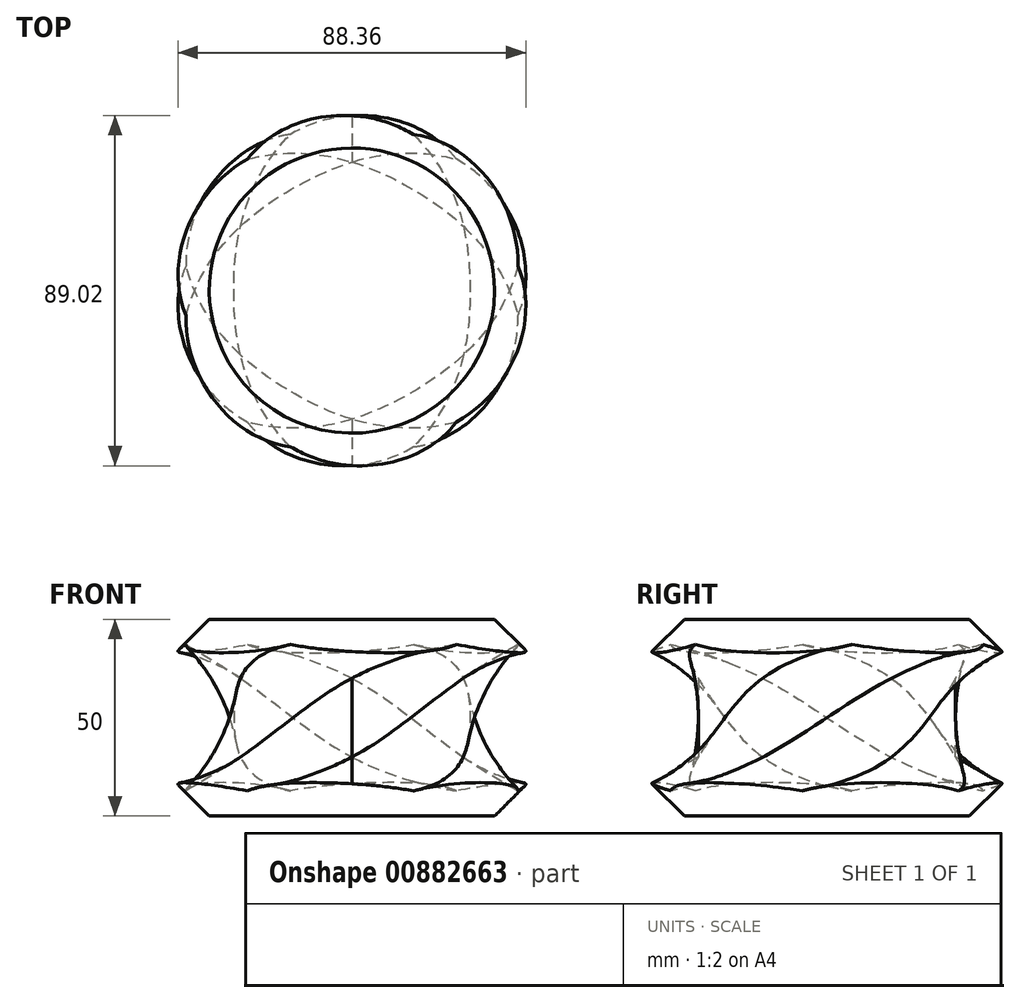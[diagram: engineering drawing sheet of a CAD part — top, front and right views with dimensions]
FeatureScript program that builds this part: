
annotation { "Feature Type Name" : "Feature", "Feature Type Description" : "" }
export const myFeature = defineFeature(function(context is Context, id is Id, definition is map)
    precondition{}
    {
        {
            var Q0;
            Q0=qCreatedBy(makeId("Front.planeOp"),FACE);
            var sketch = newSketch(context, id + "F0", { "sketchPlane" : qUnion([Q0])});
            skCircle(sketch, "E0.cCircle", {"center": v(-50, 0) * mm, "radius": 17.32 * mm, "construction": true});
            skLineSegment(sketch, "E0.0", {"start": v(-60, 17.32) * mm, "end": v(-40, 17.32) * mm});
            skLineSegment(sketch, "E0.1", {"start": v(-40, 17.32) * mm, "end": v(-30, 0) * mm});
            skLineSegment(sketch, "E0.2", {"start": v(-30, 0) * mm, "end": v(-40, -17.32) * mm});
            skLineSegment(sketch, "E0.3", {"start": v(-40, -17.32) * mm, "end": v(-60, -17.32) * mm});
            skLineSegment(sketch, "E0.4", {"start": v(-60, -17.32) * mm, "end": v(-70, 0) * mm});
            skLineSegment(sketch, "E0.5", {"start": v(-70, 0) * mm, "end": v(-60, 17.32) * mm});
            skPoint(sketch, "E0.0.midPoint", {"position": v(-50, 17.32) * mm});
            skLineSegment(sketch, "E1", {"start": v(0, 0) * mm, "end": v(-30.77, 0) * mm, "construction": true});
            skLineSegment(sketch, "E2", {"start": v(0, 0) * mm, "end": v(0, 28.34) * mm, "construction": true});
            skCircle(sketch, "E3.cCircle", {"center": v(50, 0) * mm, "radius": 17.32 * mm, "construction": true});
            skLineSegment(sketch, "E3.0", {"start": v(60, -17.32) * mm, "end": v(40, -17.32) * mm});
            skLineSegment(sketch, "E3.1", {"start": v(40, -17.32) * mm, "end": v(30, 0) * mm});
            skLineSegment(sketch, "E3.2", {"start": v(30, 0) * mm, "end": v(40, 17.32) * mm});
            skLineSegment(sketch, "E3.3", {"start": v(40, 17.32) * mm, "end": v(60, 17.32) * mm});
            skLineSegment(sketch, "E3.4", {"start": v(60, 17.32) * mm, "end": v(70, 0) * mm});
            skLineSegment(sketch, "E3.5", {"start": v(70, 0) * mm, "end": v(60, -17.32) * mm});
            skPoint(sketch, "E3.0.midPoint", {"position": v(50, -17.32) * mm});
            skSolve(sketch);
        }
        {
            var Q0;
            Q0=sQuery(id+"F0.wireOp",EDGE,"E2");
            var Q1;
            Q1=sQuery(id+"F0.wireOp",EDGE,"E1");
            cPlane(context, id + "F1", {"entities" : qUnion([Q0, Q1]), "cplaneType" : CPlaneType.LINE_ANGLE, "offset" : 150 * mm, "angle" : 150 * degree, "width" : 150 * mm, "height" : 150 * mm});
        }
        {
            var Q0;
            Q0=sQuery(id+"F0.wireOp",EDGE,"E2");
            var Q1;
            Q1=sQuery(id+"F0.wireOp",EDGE,"E1");
            cPlane(context, id + "F2", {"entities" : qUnion([Q0, Q1]), "cplaneType" : CPlaneType.LINE_ANGLE, "offset" : 150 * mm, "angle" : 120 * degree, "width" : 150 * mm, "height" : 150 * mm});
        }
        {
            var Q0;
            Q0=sQuery(id+"F0.wireOp",EDGE,"E2");
            var Q1;
            Q1=sQuery(id+"F0.wireOp",EDGE,"E1");
            cPlane(context, id + "F3", {"entities" : qUnion([Q0, Q1]), "cplaneType" : CPlaneType.LINE_ANGLE, "offset" : 150 * mm, "angle" : 60 * degree, "width" : 150 * mm, "height" : 150 * mm});
        }
        {
            var Q0;
            Q0=sQuery(id+"F0.wireOp",EDGE,"E2");
            var Q1;
            Q1=sQuery(id+"F0.wireOp",EDGE,"E1");
            cPlane(context, id + "F4", {"entities" : qUnion([Q0, Q1]), "cplaneType" : CPlaneType.LINE_ANGLE, "offset" : 150 * mm, "angle" : 30 * degree, "width" : 150 * mm, "height" : 150 * mm});
        }
        {
            var Q0;
            Q0=qCreatedBy(id+"F1.planeOp",FACE);
            var sketch = newSketch(context, id + "F5", { "sketchPlane" : qUnion([Q0])});
            skCircle(sketch, "E4.cCircle", {"center": v(50, 0) * mm, "radius": 17.32 * mm, "construction": true});
            skLineSegment(sketch, "E4.0", {"start": v(32.68, 10) * mm, "end": v(50, 20) * mm});
            skLineSegment(sketch, "E4.1", {"start": v(50, 20) * mm, "end": v(67.32, 10) * mm});
            skLineSegment(sketch, "E4.2", {"start": v(67.32, 10) * mm, "end": v(67.32, -10) * mm});
            skLineSegment(sketch, "E4.3", {"start": v(67.32, -10) * mm, "end": v(50, -20) * mm});
            skLineSegment(sketch, "E4.4", {"start": v(50, -20) * mm, "end": v(32.68, -10) * mm});
            skLineSegment(sketch, "E4.5", {"start": v(32.68, -10) * mm, "end": v(32.68, 10) * mm});
            skPoint(sketch, "E4.0.midPoint", {"position": v(41.34, 15) * mm});
            skLineSegment(sketch, "E5.MirrorCS", {"start": v(-32.68, 10) * mm, "end": v(-50, 20) * mm});
            skPoint(sketch, "E6.MirrorP", {"position": v(-41.34, 15) * mm});
            skLineSegment(sketch, "E7.MirrorCS", {"start": v(-32.68, -10) * mm, "end": v(-32.68, 10) * mm});
            skLineSegment(sketch, "E8.MirrorCS", {"start": v(-50, -20) * mm, "end": v(-32.68, -10) * mm});
            skLineSegment(sketch, "E9.MirrorCS", {"start": v(-67.32, -10) * mm, "end": v(-50, -20) * mm});
            skLineSegment(sketch, "E10.MirrorCS", {"start": v(-67.32, 10) * mm, "end": v(-67.32, -10) * mm});
            skLineSegment(sketch, "E11.MirrorCS", {"start": v(-50, 20) * mm, "end": v(-67.32, 10) * mm});
            skCircle(sketch, "E12.MirrorC", {"center": v(-50, 0) * mm, "radius": 17.32 * mm, "construction": true});
            skSolve(sketch);
        }
        {
            var Q0;
            Q0=qCreatedBy(id+"F2.planeOp",FACE);
            var sketch = newSketch(context, id + "F6", { "sketchPlane" : qUnion([Q0])});
            skCircle(sketch, "E13.cCircle", {"center": v(50, 0) * mm, "radius": 17.32 * mm, "construction": true});
            skLineSegment(sketch, "E13.0", {"start": v(30, 0) * mm, "end": v(40, 17.32) * mm});
            skLineSegment(sketch, "E13.1", {"start": v(40, 17.32) * mm, "end": v(60, 17.32) * mm});
            skLineSegment(sketch, "E13.2", {"start": v(60, 17.32) * mm, "end": v(70, 0) * mm});
            skLineSegment(sketch, "E13.3", {"start": v(70, 0) * mm, "end": v(60, -17.32) * mm});
            skLineSegment(sketch, "E13.4", {"start": v(60, -17.32) * mm, "end": v(40, -17.32) * mm});
            skLineSegment(sketch, "E13.5", {"start": v(40, -17.32) * mm, "end": v(30, 0) * mm});
            skPoint(sketch, "E13.0.midPoint", {"position": v(35, 8.66) * mm});
            skLineSegment(sketch, "E14.MirrorCS", {"start": v(-40, 17.32) * mm, "end": v(-60, 17.32) * mm});
            skLineSegment(sketch, "E15.MirrorCS", {"start": v(-30, 0) * mm, "end": v(-40, 17.32) * mm});
            skLineSegment(sketch, "E16.MirrorCS", {"start": v(-40, -17.32) * mm, "end": v(-30, 0) * mm});
            skLineSegment(sketch, "E17.MirrorCS", {"start": v(-60, -17.32) * mm, "end": v(-40, -17.32) * mm});
            skLineSegment(sketch, "E18.MirrorCS", {"start": v(-70, 0) * mm, "end": v(-60, -17.32) * mm});
            skLineSegment(sketch, "E19.MirrorCS", {"start": v(-60, 17.32) * mm, "end": v(-70, 0) * mm});
            skCircle(sketch, "E20.MirrorC", {"center": v(-50, 0) * mm, "radius": 17.32 * mm, "construction": true});
            skPoint(sketch, "E21.MirrorP", {"position": v(-35, 8.66) * mm});
            skSolve(sketch);
        }
        {
            var Q0;
            Q0=qCreatedBy(makeId("Right.planeOp"),FACE);
            var sketch = newSketch(context, id + "F7", { "sketchPlane" : qUnion([Q0])});
            skCircle(sketch, "E22.cCircle", {"center": v(50, 0) * mm, "radius": 17.32 * mm, "construction": true});
            skLineSegment(sketch, "E22.0", {"start": v(32.68, -10) * mm, "end": v(32.68, 10) * mm});
            skLineSegment(sketch, "E22.1", {"start": v(32.68, 10) * mm, "end": v(50, 20) * mm});
            skLineSegment(sketch, "E22.2", {"start": v(50, 20) * mm, "end": v(67.32, 10) * mm});
            skLineSegment(sketch, "E22.3", {"start": v(67.32, 10) * mm, "end": v(67.32, -10) * mm});
            skLineSegment(sketch, "E22.4", {"start": v(67.32, -10) * mm, "end": v(50, -20) * mm});
            skLineSegment(sketch, "E22.5", {"start": v(50, -20) * mm, "end": v(32.68, -10) * mm});
            skPoint(sketch, "E22.0.midPoint", {"position": v(32.68, 0) * mm});
            skLineSegment(sketch, "E23", {"start": v(0, 0) * mm, "end": v(18.07, 0) * mm, "construction": true});
            skLineSegment(sketch, "E24.MirrorCS", {"start": v(-50, 20) * mm, "end": v(-67.32, 10) * mm});
            skLineSegment(sketch, "E25.MirrorCS", {"start": v(-67.32, 10) * mm, "end": v(-67.32, -10) * mm});
            skLineSegment(sketch, "E26.MirrorCS", {"start": v(-67.32, -10) * mm, "end": v(-50, -20) * mm});
            skLineSegment(sketch, "E27.MirrorCS", {"start": v(-50, -20) * mm, "end": v(-32.68, -10) * mm});
            skPoint(sketch, "E28.MirrorP", {"position": v(-32.68, 0) * mm});
            skCircle(sketch, "E29.MirrorC", {"center": v(-50, 0) * mm, "radius": 17.32 * mm, "construction": true});
            skLineSegment(sketch, "E30.MirrorCS", {"start": v(-32.68, -10) * mm, "end": v(-32.68, 10) * mm});
            skLineSegment(sketch, "E31.MirrorCS", {"start": v(-32.68, 10) * mm, "end": v(-50, 20) * mm});
            skSolve(sketch);
        }
        {
            var Q0;
            Q0=qCreatedBy(id+"F3.planeOp",FACE);
            var sketch = newSketch(context, id + "F8", { "sketchPlane" : qUnion([Q0])});
            skCircle(sketch, "E32.cCircle", {"center": v(50, 0) * mm, "radius": 17.32 * mm, "construction": true});
            skLineSegment(sketch, "E32.0", {"start": v(40, -17.32) * mm, "end": v(30, 0) * mm});
            skLineSegment(sketch, "E32.1", {"start": v(30, 0) * mm, "end": v(40, 17.32) * mm});
            skLineSegment(sketch, "E32.2", {"start": v(40, 17.32) * mm, "end": v(60, 17.32) * mm});
            skLineSegment(sketch, "E32.3", {"start": v(60, 17.32) * mm, "end": v(70, 0) * mm});
            skLineSegment(sketch, "E32.4", {"start": v(70, 0) * mm, "end": v(60, -17.32) * mm});
            skLineSegment(sketch, "E32.5", {"start": v(60, -17.32) * mm, "end": v(40, -17.32) * mm});
            skPoint(sketch, "E32.0.midPoint", {"position": v(35, -8.66) * mm});
            skLineSegment(sketch, "E33.MirrorCS", {"start": v(-40, -17.32) * mm, "end": v(-30, 0) * mm});
            skCircle(sketch, "E34.MirrorC", {"center": v(-50, 0) * mm, "radius": 17.32 * mm, "construction": true});
            skPoint(sketch, "E35.MirrorP", {"position": v(-35, -8.66) * mm});
            skLineSegment(sketch, "E36.MirrorCS", {"start": v(-60, -17.32) * mm, "end": v(-40, -17.32) * mm});
            skLineSegment(sketch, "E37.MirrorCS", {"start": v(-70, 0) * mm, "end": v(-60, -17.32) * mm});
            skLineSegment(sketch, "E38.MirrorCS", {"start": v(-60, 17.32) * mm, "end": v(-70, 0) * mm});
            skLineSegment(sketch, "E39.MirrorCS", {"start": v(-40, 17.32) * mm, "end": v(-60, 17.32) * mm});
            skLineSegment(sketch, "E40.MirrorCS", {"start": v(-30, 0) * mm, "end": v(-40, 17.32) * mm});
            skSolve(sketch);
        }
        {
            var Q0;
            Q0=qCreatedBy(id+"F4.planeOp",FACE);
            var sketch = newSketch(context, id + "F9", { "sketchPlane" : qUnion([Q0])});
            skCircle(sketch, "E41.cCircle", {"center": v(50, 0) * mm, "radius": 17.32 * mm, "construction": true});
            skLineSegment(sketch, "E41.0", {"start": v(50, -20) * mm, "end": v(32.68, -10) * mm});
            skLineSegment(sketch, "E41.1", {"start": v(32.68, -10) * mm, "end": v(32.68, 10) * mm});
            skLineSegment(sketch, "E41.2", {"start": v(32.68, 10) * mm, "end": v(50, 20) * mm});
            skLineSegment(sketch, "E41.3", {"start": v(50, 20) * mm, "end": v(67.32, 10) * mm});
            skLineSegment(sketch, "E41.4", {"start": v(67.32, 10) * mm, "end": v(67.32, -10) * mm});
            skLineSegment(sketch, "E41.5", {"start": v(67.32, -10) * mm, "end": v(50, -20) * mm});
            skPoint(sketch, "E41.0.midPoint", {"position": v(41.34, -15) * mm});
            skLineSegment(sketch, "E42.MirrorCS", {"start": v(-67.32, -10) * mm, "end": v(-50, -20) * mm});
            skLineSegment(sketch, "E43.MirrorCS", {"start": v(-50, 20) * mm, "end": v(-67.32, 10) * mm});
            skLineSegment(sketch, "E44.MirrorCS", {"start": v(-50, -20) * mm, "end": v(-32.68, -10) * mm});
            skLineSegment(sketch, "E45.MirrorCS", {"start": v(-67.32, 10) * mm, "end": v(-67.32, -10) * mm});
            skLineSegment(sketch, "E46.MirrorCS", {"start": v(-32.68, 10) * mm, "end": v(-50, 20) * mm});
            skLineSegment(sketch, "E47.MirrorCS", {"start": v(-32.68, -10) * mm, "end": v(-32.68, 10) * mm});
            skCircle(sketch, "E48.MirrorC", {"center": v(-50, 0) * mm, "radius": 17.32 * mm, "construction": true});
            skPoint(sketch, "E49.MirrorP", {"position": v(-41.34, -15) * mm});
            skSolve(sketch);
        }
        {
            var Q0;
            Q0=makeQuery(id+"F0.imprint","IMPRINT",FACE,{"disambiguationData":[TD([[makeQuery(id+"F0.imprint","IMPRINT",EDGE,{"derivedFrom":sQuery(id+"F0.wireOp",EDGE,"E0.0")}),-1.0]])]});
            var Q1;
            Q1=makeQuery(id+"F5.imprint","IMPRINT",FACE,{"disambiguationData":[TD([[makeQuery(id+"F5.imprint","IMPRINT",EDGE,{"derivedFrom":sQuery(id+"F5.wireOp",EDGE,"E4.0")}),-1.0]])]});
            var Q2;
            Q2=makeQuery(id+"F6.imprint","IMPRINT",FACE,{"disambiguationData":[TD([[makeQuery(id+"F6.imprint","IMPRINT",EDGE,{"derivedFrom":sQuery(id+"F6.wireOp",EDGE,"E13.0")}),-1.0]])]});
            var Q3;
            Q3=makeQuery(id+"F7.imprint","IMPRINT",FACE,{"disambiguationData":[TD([[makeQuery(id+"F7.imprint","IMPRINT",EDGE,{"derivedFrom":sQuery(id+"F7.wireOp",EDGE,"E22.0")}),-1.0]])]});
            var Q4;
            Q4=makeQuery(id+"F8.imprint","IMPRINT",FACE,{"disambiguationData":[TD([[makeQuery(id+"F8.imprint","IMPRINT",EDGE,{"derivedFrom":sQuery(id+"F8.wireOp",EDGE,"E32.0")}),-1.0]])]});
            var Q5;
            Q5=makeQuery(id+"F9.imprint","IMPRINT",FACE,{"disambiguationData":[TD([[makeQuery(id+"F9.imprint","IMPRINT",EDGE,{"derivedFrom":sQuery(id+"F9.wireOp",EDGE,"E41.0")}),-1.0]])]});
            var Q6;
            Q6=makeQuery(id+"F0.imprint","IMPRINT",FACE,{"disambiguationData":[TD([[makeQuery(id+"F0.imprint","IMPRINT",EDGE,{"derivedFrom":sQuery(id+"F0.wireOp",EDGE,"E3.0")}),-1.0]])]});
            var Q7;
            Q7=makeQuery(id+"F5.imprint","IMPRINT",FACE,{"disambiguationData":[TD([[makeQuery(id+"F5.imprint","IMPRINT",EDGE,{"derivedFrom":sQuery(id+"F5.wireOp",EDGE,"E5.MirrorCS")}),1.0]])]});
            var Q8;
            Q8=makeQuery(id+"F6.imprint","IMPRINT",FACE,{"disambiguationData":[TD([[makeQuery(id+"F6.imprint","IMPRINT",EDGE,{"derivedFrom":sQuery(id+"F6.wireOp",EDGE,"E14.MirrorCS")}),1.0]])]});
            var Q9;
            Q9=makeQuery(id+"F7.imprint","IMPRINT",FACE,{"disambiguationData":[TD([[makeQuery(id+"F7.imprint","IMPRINT",EDGE,{"derivedFrom":sQuery(id+"F7.wireOp",EDGE,"E24.MirrorCS")}),1.0]])]});
            var Q10;
            Q10=makeQuery(id+"F8.imprint","IMPRINT",FACE,{"disambiguationData":[TD([[makeQuery(id+"F8.imprint","IMPRINT",EDGE,{"derivedFrom":sQuery(id+"F8.wireOp",EDGE,"E33.MirrorCS")}),1.0]])]});
            var Q11;
            Q11=makeQuery(id+"F9.imprint","IMPRINT",FACE,{"disambiguationData":[TD([[makeQuery(id+"F9.imprint","IMPRINT",EDGE,{"derivedFrom":sQuery(id+"F9.wireOp",EDGE,"E42.MirrorCS")}),1.0]])]});
            var Q12;
            Q12=sQuery(id+"F5.wireOp",VERTEX,"E4.5.end");
            var Q13;
            Q13=sQuery(id+"F6.wireOp",VERTEX,"E13.5.end");
            var Q14;
            Q14=sQuery(id+"F7.wireOp",VERTEX,"E22.0.start");
            var Q15;
            Q15=sQuery(id+"F8.wireOp",VERTEX,"E32.0.start");
            var Q16;
            Q16=sQuery(id+"F9.wireOp",VERTEX,"E41.0.start");
            var Q17;
            Q17=sQuery(id+"F0.wireOp",VERTEX,"E3.5.end");
            var Q18;
            Q18=sQuery(id+"F5.wireOp",VERTEX,"E9.MirrorCS.start");
            var Q19;
            Q19=sQuery(id+"F6.wireOp",VERTEX,"E19.MirrorCS.end");
            var Q20;
            Q20=sQuery(id+"F7.wireOp",VERTEX,"E24.MirrorCS.end");
            var Q21;
            Q21=sQuery(id+"F8.wireOp",VERTEX,"E38.MirrorCS.start");
            var Q22;
            Q22=sQuery(id+"F9.wireOp",VERTEX,"E43.MirrorCS.start");
            var Q23;
            Q23=sQuery(id+"F0.wireOp",VERTEX,"E0.1.start");
            loft(context, id + "F10", {"sheetProfilesArray" : [{ "sheetProfileEntities" : qUnion([Q0]) }, { "sheetProfileEntities" : qUnion([Q1]) }, { "sheetProfileEntities" : qUnion([Q2]) }, { "sheetProfileEntities" : qUnion([Q3]) }, { "sheetProfileEntities" : qUnion([Q4]) }, { "sheetProfileEntities" : qUnion([Q5]) }, { "sheetProfileEntities" : qUnion([Q6]) }, { "sheetProfileEntities" : qUnion([Q7]) }, { "sheetProfileEntities" : qUnion([Q8]) }, { "sheetProfileEntities" : qUnion([Q9]) }, { "sheetProfileEntities" : qUnion([Q10]) }, { "sheetProfileEntities" : qUnion([Q11]) }], "matchConnections" : true, "connections" : [{ "connectionEntities" : qUnion([Q12, Q13, Q14, Q15, Q16, Q17, Q18, Q19, Q20, Q21, Q22, Q23]), "connectionEdgeQueries" : qUnion([]), "connectionEdgeParameters" : [] }]});
        }
        {
            var Q0;
            Q0=qCreatedBy(makeId("Top.planeOp"),FACE);
            var sketch = newSketch(context, id + "F11", { "sketchPlane" : qUnion([Q0])});
            skLineSegment(sketch, "E50.bottom", {"start": v(0, 136.4) * mm, "end": v(167.03, 136.4) * mm});
            skLineSegment(sketch, "E50.top", {"start": v(0, -146.45) * mm, "end": v(167.03, -146.45) * mm});
            skLineSegment(sketch, "E50.left", {"start": v(0, 136.4) * mm, "end": v(0, -146.45) * mm});
            skLineSegment(sketch, "E50.right", {"start": v(167.03, 136.4) * mm, "end": v(167.03, -146.45) * mm});
            skSolve(sketch);
        }
        {
            var Q0;
            Q0=makeQuery(id+"F11.imprint","IMPRINT",FACE,{"disambiguationData":[TD([[makeQuery(id+"F11.imprint","IMPRINT",EDGE,{"derivedFrom":sQuery(id+"F11.wireOp",EDGE,"E50.bottom")}),-1.0]])]});
            extrude(context, id + "F12", {"entities" : qUnion([Q0]), "operationType" : NewBodyOperationType.INTERSECT, "endBound" : BoundingType.THROUGH_ALL, "depth" : 25 * mm, "hasSecondDirection" : true, "secondDirectionBound" : SecondDirectionBoundingType.THROUGH_ALL, "secondDirectionOppositeDirection" : true, "secondDirectionDepth" : 25 * mm});
        }
        {
            var Q0;
            Q0=makeQuery(id+"F10.opLoft","SWEPT_BODY",BODY,{"disambiguationData":[OSD([sQuery(id+"F0.wireOp",EDGE,"E3.0"),makeQuery(id+"F0.imprint","IMPRINT",FACE,{"disambiguationData":[TD([[makeQuery(id+"F0.imprint","IMPRINT",EDGE,{"derivedFrom":sQuery(id+"F0.wireOp",EDGE,"E0.0")}),-1.0]])]}),sQuery(id+"F5.wireOp",EDGE,"E4.0"),sQuery(id+"F5.wireOp",EDGE,"E9.MirrorCS"),sQuery(id+"F6.wireOp",EDGE,"E13.0"),sQuery(id+"F6.wireOp",EDGE,"E17.MirrorCS"),sQuery(id+"F7.wireOp",EDGE,"E22.0"),sQuery(id+"F7.wireOp",EDGE,"E27.MirrorCS"),sQuery(id+"F8.wireOp",EDGE,"E32.0"),sQuery(id+"F8.wireOp",EDGE,"E38.MirrorCS"),sQuery(id+"F9.wireOp",EDGE,"E41.0"),makeQuery(id+"F9.imprint","IMPRINT",FACE,{"disambiguationData":[TD([[makeQuery(id+"F9.imprint","IMPRINT",EDGE,{"derivedFrom":sQuery(id+"F9.wireOp",EDGE,"E42.MirrorCS")}),1.0]])]})])]});
            var Q1;
            Q1=sQuery(id+"F0.wireOp",EDGE,"E2");
            circularPattern(context, id + "F13", {"operationType" : NewBodyOperationType.ADD, "entities" : qUnion([Q0]), "axis" : qUnion([Q1]), "angle" : 180 * degree, "instanceCount" : 2});
        }
        {
            var Q0;
            Q0=qCreatedBy(makeId("Front.planeOp"),FACE);
            var sketch = newSketch(context, id + "F14", { "sketchPlane" : qUnion([Q0])});
            skLineSegment(sketch, "E51.0", {"start": v(-40, 17.32) * mm, "end": v(-30, 0) * mm, "construction": true});
            skLineSegment(sketch, "E51.1", {"start": v(-30, 0) * mm, "end": v(-40, -17.32) * mm, "construction": true});
            skLineSegment(sketch, "E51.2", {"start": v(-40, -17.32) * mm, "end": v(-60, -17.32) * mm, "construction": true});
            skLineSegment(sketch, "E51.3", {"start": v(-60, -17.32) * mm, "end": v(-70, 0) * mm, "construction": true});
            skLineSegment(sketch, "E51.4", {"start": v(-70, 0) * mm, "end": v(-60, 17.32) * mm, "construction": true});
            skLineSegment(sketch, "E51.5", {"start": v(-60, 17.32) * mm, "end": v(-40, 17.32) * mm, "construction": true});
            skCircle(sketch, "E51.6", {"center": v(-50, 0) * mm, "radius": 17.32 * mm});
            skCircle(sketch, "E52", {"center": v(-50, 0) * mm, "radius": 20 * mm});
            skSolve(sketch);
        }
        {
            var Q0;
            Q0=makeQuery(id+"F14.imprint","IMPRINT",FACE,{"disambiguationData":[TD([[makeQuery(id+"F14.imprint","IMPRINT",EDGE,{"derivedFrom":sQuery(id+"F14.wireOp",EDGE,"E52")}),1.0]])]});
            var Q1;
            Q1=sQuery(id+"F0.wireOp",EDGE,"E2");
            revolve(context, id + "F15", {"entities" : qUnion([Q0]), "axis" : qUnion([Q1]), "revolveType" : RevolveType.FULL});
        }
        {
            var Q0;
            Q0=makeQuery(id+"F15.opRevolve","SWEPT_BODY",BODY,{"disambiguationData":[OSD([sQuery(id+"F14.wireOp",EDGE,"E52")])]});
            deleteBodies(context, id + "F16", {"entities" : qUnion([Q0])});
        }
        {
            var Q0;
            Q0=makeQuery(id+"F14.imprint","IMPRINT",FACE,{"disambiguationData":[TD([[makeQuery(id+"F14.imprint","IMPRINT",EDGE,{"derivedFrom":sQuery(id+"F14.wireOp",EDGE,"E51.6")}),1.0]])]});
            var Q1;
            Q1=sQuery(id+"F0.wireOp",EDGE,"E2");
            revolve(context, id + "F17", {"entities" : qUnion([Q0]), "axis" : qUnion([Q1]), "revolveType" : RevolveType.FULL});
        }
        {
            var Q0;
            Q0=makeQuery(id+"F17.opRevolve","SWEPT_BODY",BODY,{"disambiguationData":[OSD([sQuery(id+"F14.wireOp",EDGE,"E51.6")])]});
            deleteBodies(context, id + "F18", {"entities" : qUnion([Q0])});
        }
        {
            var Q0;
            Q0=qCreatedBy(makeId("Top.planeOp"),FACE);
            var sketch = newSketch(context, id + "F19", { "sketchPlane" : qUnion([Q0])});
            skCircle(sketch, "E53", {"center": v(0, 0) * mm, "radius": 46.24 * mm});
            skSolve(sketch);
        }
        {
            var Q0;
            Q0=makeQuery(id+"F19.imprint","IMPRINT",FACE,{"disambiguationData":[TD([[makeQuery(id+"F19.imprint","IMPRINT",EDGE,{"derivedFrom":sQuery(id+"F19.wireOp",EDGE,"E53")}),1.0]])]});
            extrude(context, id + "F20", {"entities" : qUnion([Q0]), "endBound" : BoundingType.SYMMETRIC, "depth" : 50 * mm});
        }
        {
            var Q0;
            Q0=makeQuery(id+"F20.opExtrude","CAP_EDGE",EDGE,{"disambiguationData":[OSD([sQuery(id+"F19.wireOp",EDGE,"E53")])],"isStart":false});
            var Q1;
            Q1=makeQuery(id+"F20.opExtrude","CAP_EDGE",EDGE,{"disambiguationData":[OSD([sQuery(id+"F19.wireOp",EDGE,"E53")])],"isStart":true});
            chamfer(context, id + "F21", {"entities" : qUnion([Q0, Q1]), "width" : 10 * mm, "tangentPropagation" : true});
        }
        {
            var Q0;
            Q0=makeQuery(id+"F10.opLoft","SWEPT_BODY",BODY,{"disambiguationData":[OSD([sQuery(id+"F0.wireOp",EDGE,"E3.0"),makeQuery(id+"F0.imprint","IMPRINT",FACE,{"disambiguationData":[TD([[makeQuery(id+"F0.imprint","IMPRINT",EDGE,{"derivedFrom":sQuery(id+"F0.wireOp",EDGE,"E0.0")}),-1.0]])]}),sQuery(id+"F5.wireOp",EDGE,"E4.0"),sQuery(id+"F5.wireOp",EDGE,"E9.MirrorCS"),sQuery(id+"F6.wireOp",EDGE,"E13.0"),sQuery(id+"F6.wireOp",EDGE,"E17.MirrorCS"),sQuery(id+"F7.wireOp",EDGE,"E22.0"),sQuery(id+"F7.wireOp",EDGE,"E27.MirrorCS"),sQuery(id+"F8.wireOp",EDGE,"E32.0"),sQuery(id+"F8.wireOp",EDGE,"E38.MirrorCS"),sQuery(id+"F9.wireOp",EDGE,"E41.0"),makeQuery(id+"F9.imprint","IMPRINT",FACE,{"disambiguationData":[TD([[makeQuery(id+"F9.imprint","IMPRINT",EDGE,{"derivedFrom":sQuery(id+"F9.wireOp",EDGE,"E42.MirrorCS")}),1.0]])]})])]});
            var Q1;
            Q1=makeQuery(id+"F20.opExtrude","SWEPT_BODY",BODY,{"disambiguationData":[OSD([sQuery(id+"F19.wireOp",EDGE,"E53")])]});
            booleanBodies(context, id + "F22", {"operationType" : BooleanOperationType.SUBTRACTION, "tools" : qUnion([Q0]), "targets" : qUnion([Q1])});
        }
    });
